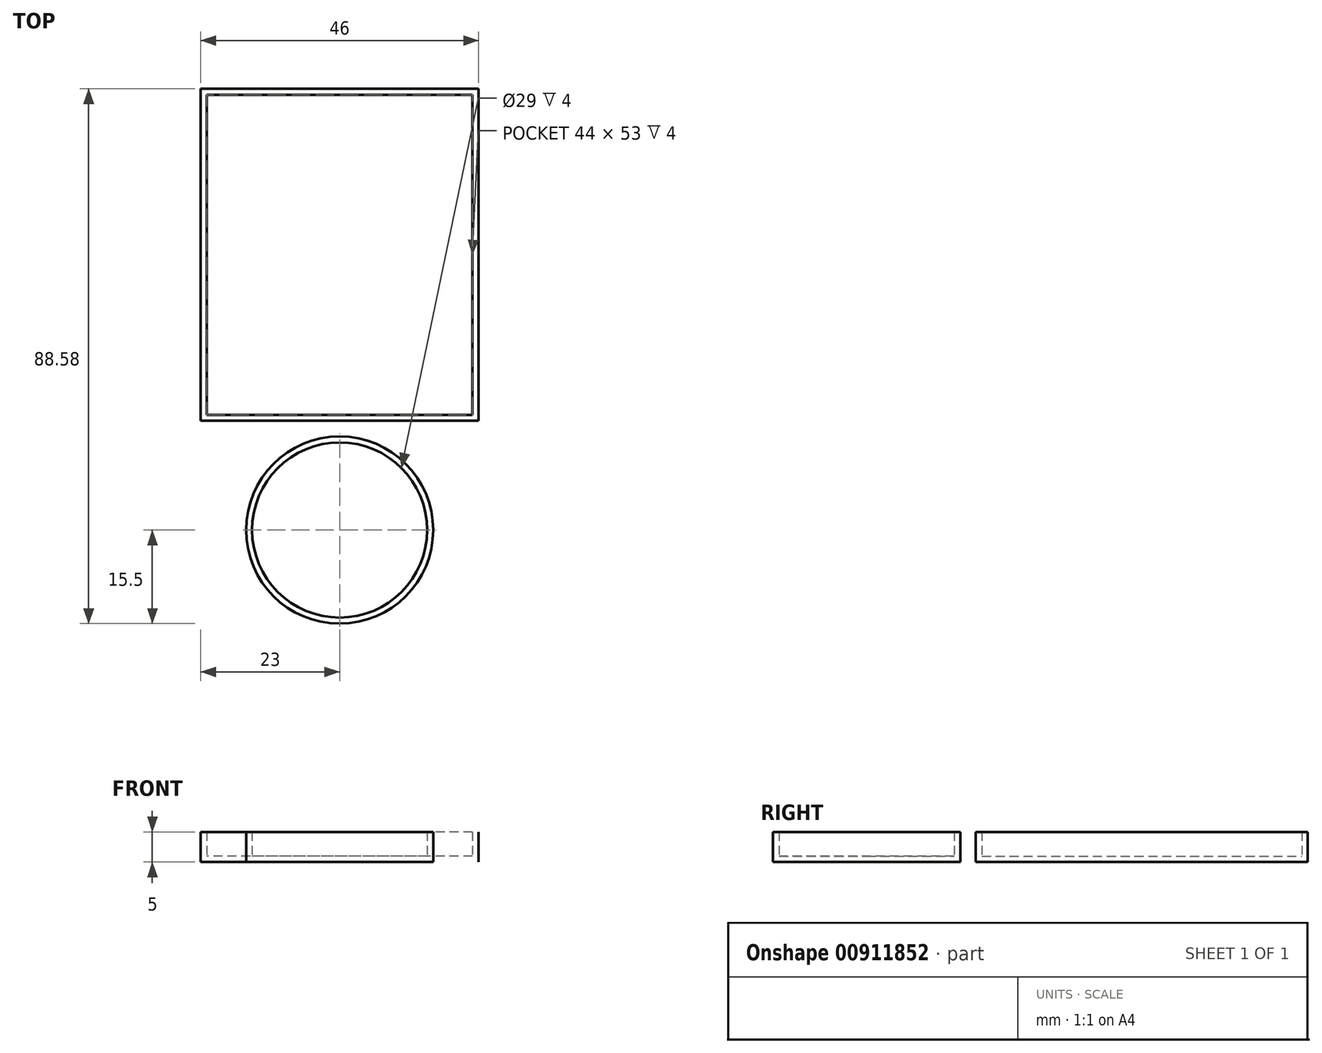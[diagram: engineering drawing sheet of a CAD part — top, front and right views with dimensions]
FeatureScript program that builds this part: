
annotation { "Feature Type Name" : "Feature", "Feature Type Description" : "" }
export const myFeature = defineFeature(function(context is Context, id is Id, definition is map)
    precondition{}
    {
        {
            var Q0;
            Q0=qCreatedBy(makeId("Top.planeOp"),FACE);
            var sketch = newSketch(context, id + "F0", { "sketchPlane" : qUnion([Q0])});
            skCircle(sketch, "E0", {"center": v(0, 0) * mm, "radius": 15.5 * mm});
            skLineSegment(sketch, "E1.bottom", {"start": v(23, 18.08) * mm, "end": v(-23, 18.08) * mm});
            skLineSegment(sketch, "E1.top", {"start": v(23, 73.08) * mm, "end": v(-23, 73.08) * mm});
            skLineSegment(sketch, "E1.left", {"start": v(23, 18.08) * mm, "end": v(23, 73.08) * mm});
            skLineSegment(sketch, "E1.right", {"start": v(-23, 18.08) * mm, "end": v(-23, 73.08) * mm});
            skPoint(sketch, "E1.middle", {"position": v(0, 45.58) * mm});
            skSolve(sketch);
        }
        {
            var Q0;
            Q0=makeQuery(id+"F0.imprint","IMPRINT",FACE,{"disambiguationData":[TD([[makeQuery(id+"F0.imprint","IMPRINT",EDGE,{"derivedFrom":sQuery(id+"F0.wireOp",EDGE,"E0")}),1.0]])]});
            var Q1;
            Q1=makeQuery(id+"F0.imprint","IMPRINT",FACE,{"disambiguationData":[TD([[makeQuery(id+"F0.imprint","IMPRINT",EDGE,{"derivedFrom":sQuery(id+"F0.wireOp",EDGE,"E1.bottom")}),-1.0]])]});
            extrude(context, id + "F1", {"entities" : qUnion([Q0, Q1]), "depth" : 5 * mm, "offsetDistance" : 25 * mm});
        }
        {
            var Q0;
            Q0=makeQuery(id+"F1.opExtrude","CAP_FACE",FACE,{"disambiguationData":[OSD([sQuery(id+"F0.wireOp",EDGE,"E0")])],"isStart":false});
            var Q1;
            Q1=makeQuery(id+"F1.opExtrude","CAP_FACE",FACE,{"disambiguationData":[OSD([sQuery(id+"F0.wireOp",EDGE,"E1.bottom"),sQuery(id+"F0.wireOp",EDGE,"E1.top"),sQuery(id+"F0.wireOp",EDGE,"E1.left"),sQuery(id+"F0.wireOp",EDGE,"E1.right")])],"isStart":false});
            shell(context, id + "F2", {"entities" : qUnion([Q0, Q1]), "thickness" : 1 * mm});
        }
    });
